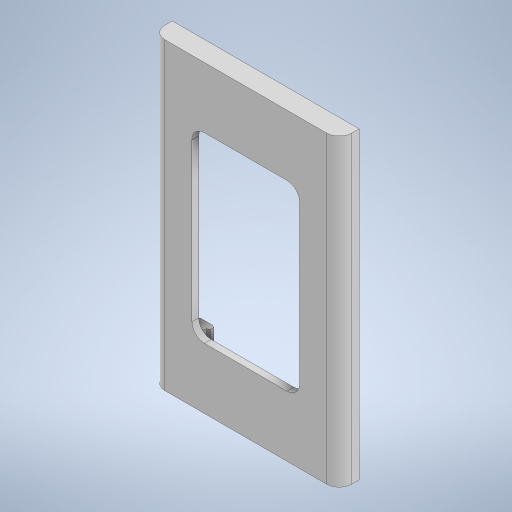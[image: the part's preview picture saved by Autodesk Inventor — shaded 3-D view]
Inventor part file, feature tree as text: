
AUTODESK INVENTOR PART (.ipt)
format: ipt  version: 2023 (Build 270158000, 158)  size: 361,472 bytes
history: native  units: mm
features: sketch x5, extrude x4, fillet x3, other x2, chamfer x2, mirror x2, shell x1
ambient origin geometry x8: Origin, YZ Plane, XZ Plane, XY Plane, X Axis, Y Axis, Z Axis, Center Point
bodies: Body1 (feature_tree)
feature tree (19):
  other  "솔리드1"
  extrude  "돌출1"  Depth=75.0mm
  fillet  "모깎기1"  Radius=122.0mm
  shell  "쉘1"  Thickness=43.2mm
  extrude  "돌출2"  Depth=73.2mm
  extrude  "돌출3"  Depth=8.0mm TaperAngle=0.0deg
  chamfer  "모따기1"  Distance=5.0mm
  extrude  "돌출4"  Depth=1.7mm
  mirror  "미러1"
  mirror  "미러2"
  sketch  "스케치5"
  fillet  "모깎기6"  Radius=8.0mm
  chamfer  "모따기2"  Distance=36.85mm
  other  "두껍게 하기1"
  fillet  "모깎기7"  Radius=6.9mm
  sketch  "스케치1"
  sketch  "스케치2"
  sketch  "스케치3"
  sketch  "스케치4"
